# Revit family: Internal block_450_560_DH_1R1A
name_source: partatom
category: Оборудование
units: mm (PartAtom-declared; Revit-internal decimal feet)

## family parameters
Всегда вертикально = Да
Классификация = Нет
На основе рабочей плоскости = Нет
Общий = Нет
При загрузке вырезать с полостями = Нет
Размер круглого соединителя = Использовать диаметр
Тип детали = Нормальный
Точка принадлежности помещению = Нет

## types (2) — shared parameters
00_20_Manufacturer = BLAUBERG
00_20_Name = Internal block
A = 2165 мм
B = 916 мм
Bb = 916 мм
C = 676 мм
Casing Material = Steel, galvanized
D1 = 1926 мм
D2 = 2176 мм
Db = 1926 мм
E = 950 мм
F = 928 мм
G = 292 мм
Grid Material = Mesh, steel, painted,  white
H = 1563 мм
Height = 676 мм
I = 563 мм
Length = 2165 мм
Load Classification = HVAC
Maintenance zone material = <По категории>
Maximum Air Flow = 0.0 л/с
Weight = 222.00 кг
Width = 916 мм
dd = 10 мм
dg = 29 мм
dr = 16 мм
Изготовитель = BLAUBERG
zero-valued in all types: Отметка по умолчанию

## per-type parameters (varying)
| type | Power |
| BLHV-450-I-DH-AC/1R1A | 1600 Вт |
| BLHV-560-I-DH-AC/1R1A | 2500 Вт |

note: column(s) folded — value = type name in every type: 00_20_Type
